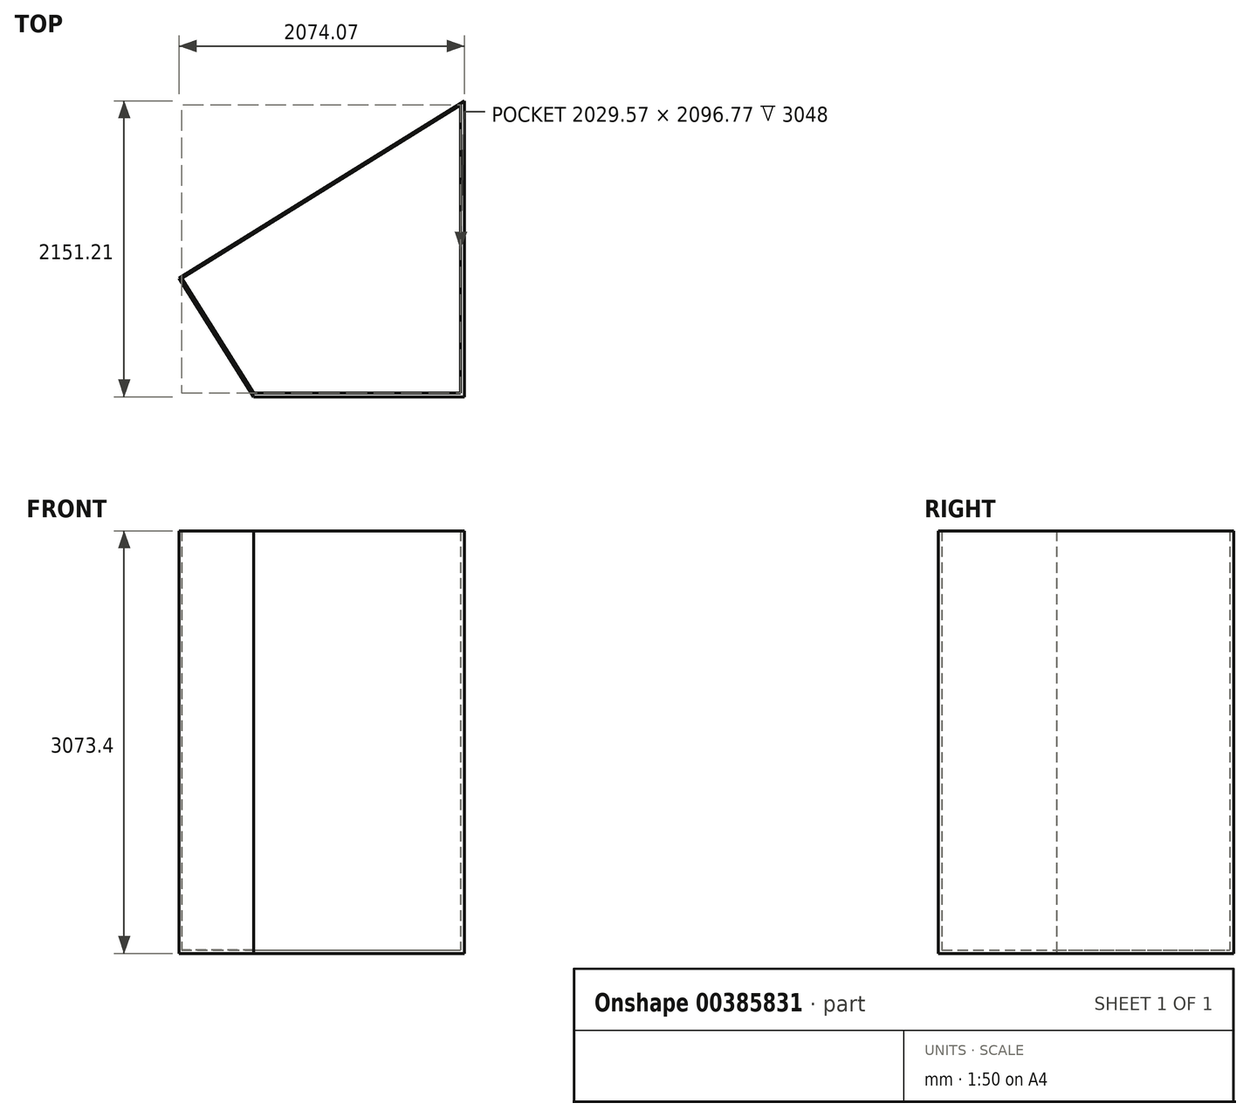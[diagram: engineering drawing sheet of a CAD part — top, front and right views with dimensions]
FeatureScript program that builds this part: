
annotation { "Feature Type Name" : "Feature", "Feature Type Description" : "" }
export const myFeature = defineFeature(function(context is Context, id is Id, definition is map)
    precondition{}
    {
        {
            var Q0;
            Q0=qCreatedBy(makeId("Top.planeOp"),FACE);
            var sketch = newSketch(context, id + "F0", { "sketchPlane" : qUnion([Q0])});
            skLineSegment(sketch, "E0", {"start": v(-196.92, 89.7) * mm, "end": v(1877.15, 1379.86) * mm});
            skLineSegment(sketch, "E1", {"start": v(1877.15, 1379.86) * mm, "end": v(1877.15, -771.35) * mm});
            skLineSegment(sketch, "E2", {"start": v(1877.15, -771.35) * mm, "end": v(343.62, -771.35) * mm});
            skLineSegment(sketch, "E3", {"start": v(343.62, -771.35) * mm, "end": v(-196.92, 89.7) * mm});
            skSolve(sketch);
        }
        {
            var Q0;
            Q0 = qSketchRegion(id + "F0", true);
            extrude(context, id + "F1", {"entities" : qUnion([Q0]), "depth" : 25.4 * mm});
        }
        {
            var Q0;
            Q0=makeQuery(id+"F1.opExtrude","CAP_FACE",FACE,{"disambiguationData":[OSD([sQuery(id+"F0.wireOp",EDGE,"E0"),sQuery(id+"F0.wireOp",EDGE,"E1"),sQuery(id+"F0.wireOp",EDGE,"E2"),sQuery(id+"F0.wireOp",EDGE,"E3")])],"isStart":false});
            var sketch = newSketch(context, id + "F2", { "sketchPlane" : qUnion([Q0])});
            skLineSegment(sketch, "E4.bottom", {"start": v(343.62, -771.35) * mm, "end": v(1877.15, -771.35) * mm});
            skLineSegment(sketch, "E4.top", {"start": v(343.62, -744.6) * mm, "end": v(1877.15, -744.6) * mm});
            skLineSegment(sketch, "E4.left", {"start": v(343.62, -771.35) * mm, "end": v(343.62, -744.6) * mm});
            skLineSegment(sketch, "E4.right", {"start": v(1877.15, -771.35) * mm, "end": v(1877.15, -744.6) * mm});
            skSolve(sketch);
        }
        {
            var Q0;
            Q0 = qSketchRegion(id + "F2", true);
            extrude(context, id + "F3", {"entities" : qUnion([Q0]), "operationType" : NewBodyOperationType.ADD, "depth" : 3048 * mm});
        }
        {
            var Q0;
            Q0=makeQuery(id+"F1.opExtrude","CAP_FACE",FACE,{"disambiguationData":[OSD([sQuery(id+"F0.wireOp",EDGE,"E0"),sQuery(id+"F0.wireOp",EDGE,"E1"),sQuery(id+"F0.wireOp",EDGE,"E2"),sQuery(id+"F0.wireOp",EDGE,"E3")])],"isStart":false});
            var sketch = newSketch(context, id + "F4", { "sketchPlane" : qUnion([Q0])});
            skLineSegment(sketch, "E5", {"start": v(-196.92, 89.7) * mm, "end": v(343.62, -771.35) * mm});
            skLineSegment(sketch, "E6", {"start": v(343.62, -771.35) * mm, "end": v(343.62, -744.6) * mm});
            skLineSegment(sketch, "E7", {"start": v(343.62, -744.6) * mm, "end": v(-180.12, 89.7) * mm});
            skLineSegment(sketch, "E8", {"start": v(-180.12, 89.7) * mm, "end": v(-196.92, 89.7) * mm});
            skSolve(sketch);
        }
        {
            var Q0;
            Q0 = qSketchRegion(id + "F4", true);
            extrude(context, id + "F5", {"entities" : qUnion([Q0]), "operationType" : NewBodyOperationType.ADD, "depth" : 3048 * mm});
        }
        {
            var Q0;
            Q0=makeQuery(id+"F1.opExtrude","CAP_FACE",FACE,{"disambiguationData":[OSD([sQuery(id+"F0.wireOp",EDGE,"E0"),sQuery(id+"F0.wireOp",EDGE,"E1"),sQuery(id+"F0.wireOp",EDGE,"E2"),sQuery(id+"F0.wireOp",EDGE,"E3")])],"isStart":false});
            var sketch = newSketch(context, id + "F6", { "sketchPlane" : qUnion([Q0])});
            skLineSegment(sketch, "E9", {"start": v(1877.15, 1379.86) * mm, "end": v(-196.92, 89.7) * mm});
            skLineSegment(sketch, "E10", {"start": v(-196.92, 89.7) * mm, "end": v(-180.12, 89.7) * mm});
            skLineSegment(sketch, "E11", {"start": v(-180.12, 89.7) * mm, "end": v(1877.15, 1369.4) * mm});
            skLineSegment(sketch, "E12", {"start": v(1877.15, 1369.4) * mm, "end": v(1877.15, 1379.86) * mm});
            skSolve(sketch);
        }
        {
            var Q0;
            Q0 = qSketchRegion(id + "F6", true);
            extrude(context, id + "F7", {"entities" : qUnion([Q0]), "operationType" : NewBodyOperationType.ADD, "depth" : 3048 * mm});
        }
        {
            var Q0;
            Q0=makeQuery(id+"F1.opExtrude","CAP_FACE",FACE,{"disambiguationData":[OSD([sQuery(id+"F0.wireOp",EDGE,"E0"),sQuery(id+"F0.wireOp",EDGE,"E1"),sQuery(id+"F0.wireOp",EDGE,"E2"),sQuery(id+"F0.wireOp",EDGE,"E3")])],"isStart":false});
            var sketch = newSketch(context, id + "F8", { "sketchPlane" : qUnion([Q0])});
            skLineSegment(sketch, "E13", {"start": v(1877.15, 1369.4) * mm, "end": v(1877.15, -744.6) * mm});
            skLineSegment(sketch, "E14", {"start": v(1877.15, -744.6) * mm, "end": v(1849.44, -744.6) * mm});
            skLineSegment(sketch, "E15", {"start": v(1849.44, -744.6) * mm, "end": v(1849.44, 1352.17) * mm});
            skLineSegment(sketch, "E16", {"start": v(1849.44, 1352.17) * mm, "end": v(1877.15, 1369.4) * mm});
            skSolve(sketch);
        }
        {
            var Q0;
            Q0 = qSketchRegion(id + "F8", true);
            extrude(context, id + "F9", {"entities" : qUnion([Q0]), "operationType" : NewBodyOperationType.ADD, "depth" : 3048 * mm});
        }
    });
